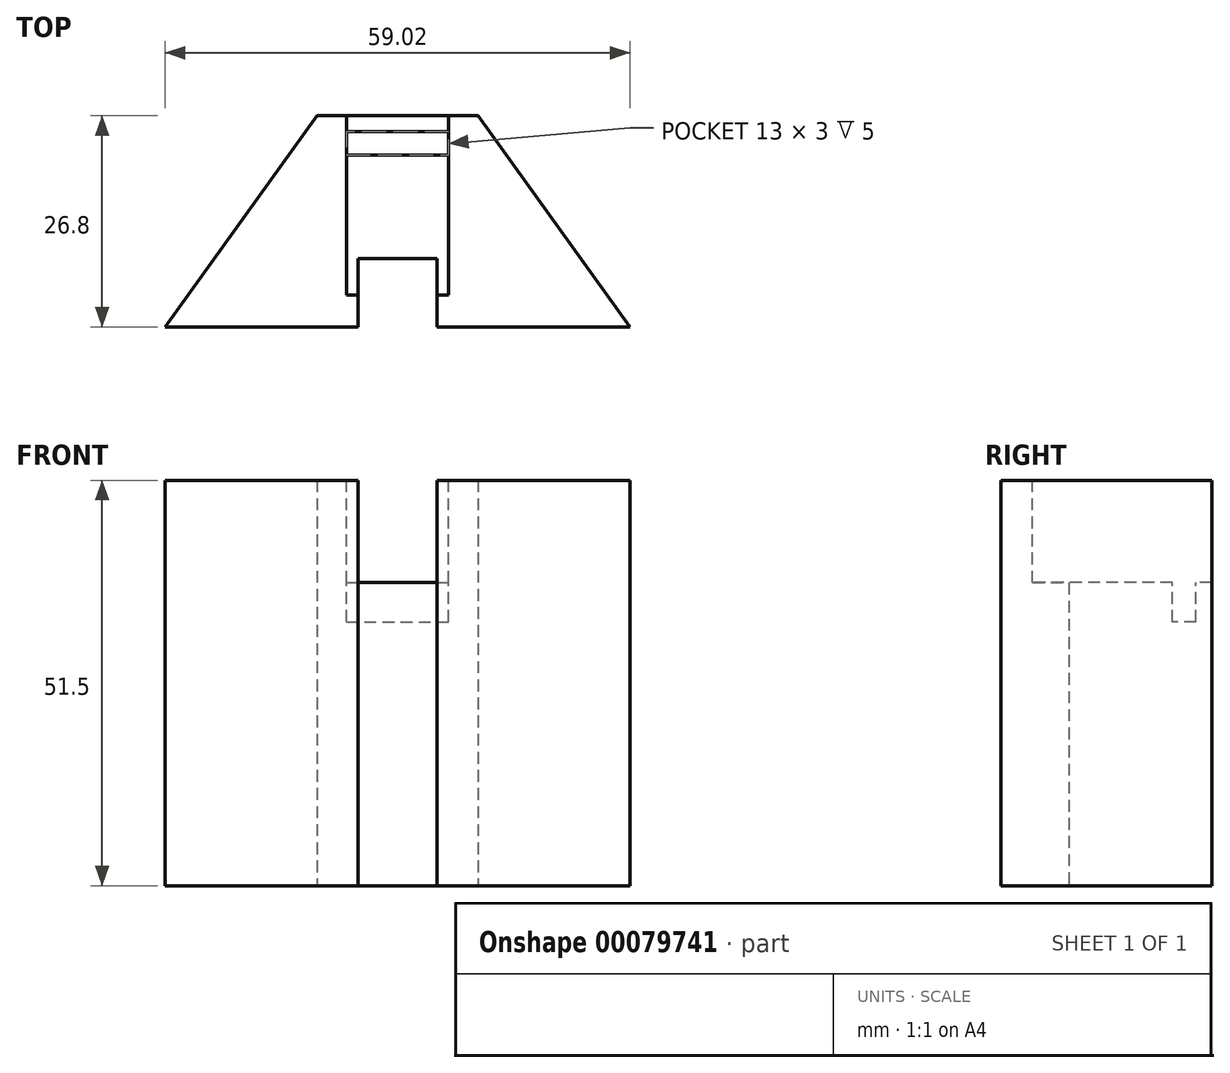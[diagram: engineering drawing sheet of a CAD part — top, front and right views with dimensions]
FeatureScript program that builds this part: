
annotation { "Feature Type Name" : "Feature", "Feature Type Description" : "" }
export const myFeature = defineFeature(function(context is Context, id is Id, definition is map)
    precondition{}
    {
        {
            var Q0;
            Q0=qCreatedBy(makeId("Top.planeOp"),FACE);
            var sketch = newSketch(context, id + "F0", { "sketchPlane" : qUnion([Q0])});
            skLineSegment(sketch, "E0", {"start": v(-29.5, 0) * mm, "end": v(-5, 0) * mm});
            skLineSegment(sketch, "E1", {"start": v(29.5, 0) * mm, "end": v(10.25, 26.8) * mm});
            skLineSegment(sketch, "E2", {"start": v(10.25, 26.8) * mm, "end": v(-10.25, 26.8) * mm});
            skLineSegment(sketch, "E3", {"start": v(-10.25, 26.8) * mm, "end": v(-29.5, 0) * mm});
            skLineSegment(sketch, "E4.top", {"start": v(5, 8.67) * mm, "end": v(-5, 8.67) * mm});
            skLineSegment(sketch, "E4.left", {"start": v(5, 0) * mm, "end": v(5, 8.67) * mm});
            skLineSegment(sketch, "E4.right", {"start": v(-5, 0) * mm, "end": v(-5, 8.67) * mm});
            skLineSegment(sketch, "E5.trimOffspring", {"start": v(5, 0) * mm, "end": v(29.5, 0) * mm});
            skSolve(sketch);
        }
        {
            var Q0;
            Q0 = qSketchRegion(id + "F0", true);
            extrude(context, id + "F1", {"entities" : qUnion([Q0]), "depth" : 51.5 * mm});
        }
        {
            var Q0;
            Q0=makeQuery(id+"F1.opExtrude","CAP_FACE",FACE,{"disambiguationData":[OSD([sQuery(id+"F0.wireOp",EDGE,"E0"),sQuery(id+"F0.wireOp",EDGE,"E1"),sQuery(id+"F0.wireOp",EDGE,"E2"),sQuery(id+"F0.wireOp",EDGE,"E3"),sQuery(id+"F0.wireOp",EDGE,"E4.top"),sQuery(id+"F0.wireOp",EDGE,"E4.left"),sQuery(id+"F0.wireOp",EDGE,"E4.right"),sQuery(id+"F0.wireOp",EDGE,"E5.trimOffspring")])],"isStart":false});
            var sketch = newSketch(context, id + "F2", { "sketchPlane" : qUnion([Q0])});
            skLineSegment(sketch, "E6.bottom", {"start": v(-6.5, 26.8) * mm, "end": v(6.5, 26.8) * mm});
            skLineSegment(sketch, "E6.top", {"start": v(-6.5, 4.05) * mm, "end": v(6.5, 4.05) * mm});
            skLineSegment(sketch, "E6.left", {"start": v(-6.5, 26.8) * mm, "end": v(-6.5, 4.05) * mm});
            skLineSegment(sketch, "E6.right", {"start": v(6.5, 26.8) * mm, "end": v(6.5, 4.05) * mm});
            skSolve(sketch);
        }
        {
            var Q0;
            Q0 = qSketchRegion(id + "F2", true);
            extrude(context, id + "F3", {"entities" : qUnion([Q0]), "operationType" : NewBodyOperationType.REMOVE, "oppositeDirection" : true, "depth" : 13 * mm});
        }
        {
            var Q0;
            Q0=makeQuery(id+"F3.boolean.opBoolean","COPY",FACE,{"derivedFrom":makeQuery(id+"F3.opExtrude","CAP_FACE",FACE,{"disambiguationData":[OSD([sQuery(id+"F2.wireOp",EDGE,"E6.bottom"),sQuery(id+"F2.wireOp",EDGE,"E6.top"),sQuery(id+"F2.wireOp",EDGE,"E6.left"),sQuery(id+"F2.wireOp",EDGE,"E6.right")])],"isStart":false})});
            var sketch = newSketch(context, id + "F4", { "sketchPlane" : qUnion([Q0])});
            skLineSegment(sketch, "E7.bottom", {"start": v(-6.5, 24.8) * mm, "end": v(6.5, 24.8) * mm});
            skLineSegment(sketch, "E7.top", {"start": v(-6.5, 21.8) * mm, "end": v(6.5, 21.8) * mm});
            skLineSegment(sketch, "E7.left", {"start": v(-6.5, 24.8) * mm, "end": v(-6.5, 21.8) * mm});
            skLineSegment(sketch, "E7.right", {"start": v(6.5, 24.8) * mm, "end": v(6.5, 21.8) * mm});
            skSolve(sketch);
        }
        {
            var Q0;
            Q0 = qSketchRegion(id + "F4", true);
            extrude(context, id + "F5", {"entities" : qUnion([Q0]), "operationType" : NewBodyOperationType.REMOVE, "oppositeDirection" : true, "depth" : 5 * mm});
        }
    });
